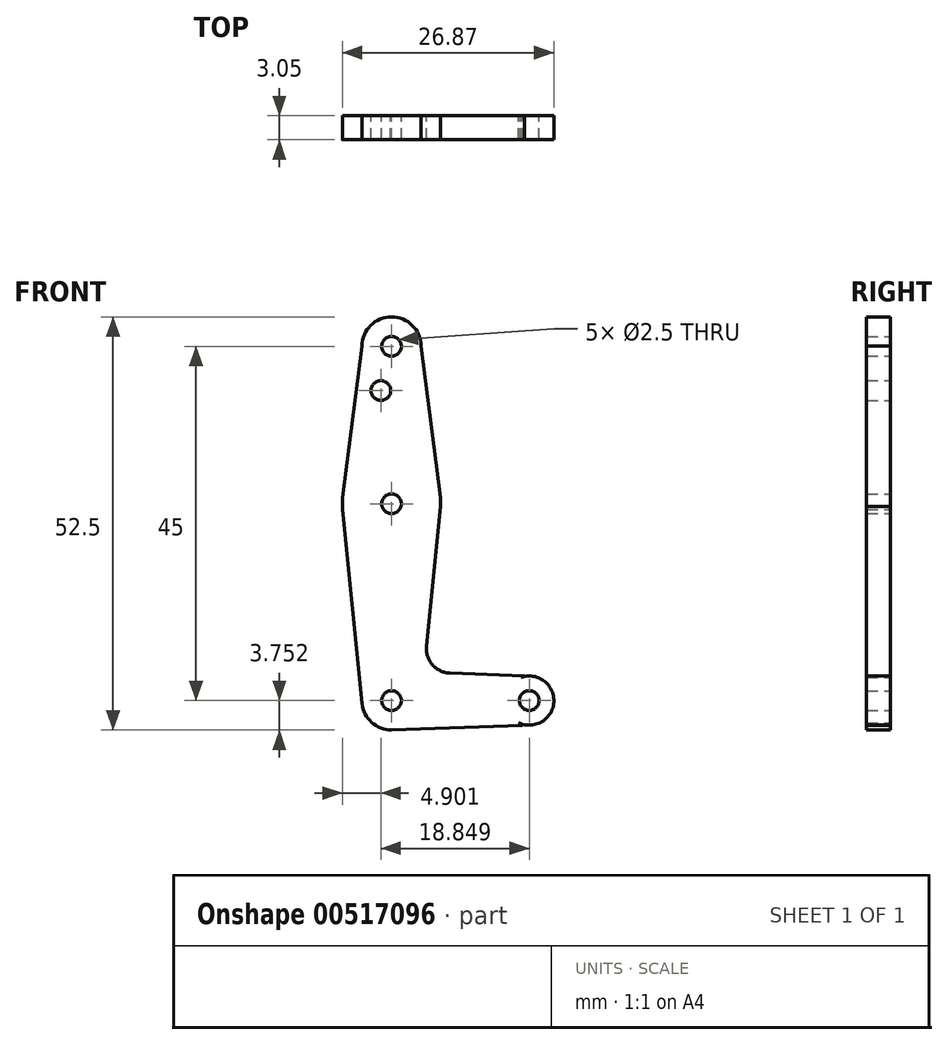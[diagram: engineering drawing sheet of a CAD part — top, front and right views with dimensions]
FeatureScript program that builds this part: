
annotation { "Feature Type Name" : "Feature", "Feature Type Description" : "" }
export const myFeature = defineFeature(function(context is Context, id is Id, definition is map)
    precondition{}
    {
        {
            var Q0;
            Q0=qCreatedBy(makeId("Front.planeOp"),FACE);
            var sketch = newSketch(context, id + "F0", { "sketchPlane" : qUnion([Q0])});
            skLineSegment(sketch, "E0", {"start": v(-17.5, -53.76) * mm, "end": v(-17.5, -28.76) * mm});
            skLineSegment(sketch, "E1", {"start": v(-17.5, -28.76) * mm, "end": v(-17.5, -8.76) * mm});
            skLineSegment(sketch, "E2", {"start": v(-17.5, -53.76) * mm, "end": v(0, -53.76) * mm});
            skCircle(sketch, "E3", {"center": v(-17.5, -8.76) * mm, "radius": 3.75 * mm});
            skCircle(sketch, "E4", {"center": v(-17.5, -28.76) * mm, "radius": 6.25 * mm});
            skCircle(sketch, "E5", {"center": v(-17.5, -53.76) * mm, "radius": 3.75 * mm});
            skCircle(sketch, "E6", {"center": v(0, -53.76) * mm, "radius": 3.12 * mm});
            skLineSegment(sketch, "E7", {"start": v(-21.25, -8.7) * mm, "end": v(-23.7, -27.97) * mm});
            skLineSegment(sketch, "E8", {"start": v(-13.75, -8.7) * mm, "end": v(-11.3, -27.97) * mm});
            skLineSegment(sketch, "E9", {"start": v(-23.7, -29.5) * mm, "end": v(-21.23, -54.13) * mm});
            skLineSegment(sketch, "E10", {"start": v(-11.26, -29.13) * mm, "end": v(-13.05, -46.83) * mm});
            skLineSegment(sketch, "E11", {"start": v(-10.05, -50.27) * mm, "end": v(0, -50.63) * mm});
            skLineSegment(sketch, "E12", {"start": v(-17.5, -57.5) * mm, "end": v(0, -56.89) * mm});
            skCircle(sketch, "E13", {"center": v(-17.5, -8.76) * mm, "radius": 1.25 * mm});
            skCircle(sketch, "E14", {"center": v(-17.5, -28.76) * mm, "radius": 1.25 * mm});
            skCircle(sketch, "E15", {"center": v(-17.5, -53.76) * mm, "radius": 1.25 * mm});
            skCircle(sketch, "E16", {"center": v(0, -53.76) * mm, "radius": 1.25 * mm});
            skArc(sketch, "E17.filletArc", {"start": v(-13.05, -46.83) * mm, "mid": v(-12.3, -49.2) * mm, "end": v(-10.05, -50.27) * mm});
            skCircle(sketch, "E18", {"center": v(-18.85, -14.38) * mm, "radius": 1.25 * mm});
            skLineSegment(sketch, "E19", {"start": v(-0.6, -50.6) * mm, "end": v(-1.03, -50.8) * mm});
            skLineSegment(sketch, "E20", {"start": v(-0.89, -56.92) * mm, "end": v(-1.35, -56.58) * mm});
            skSolve(sketch);
        }
        {
            var Q0;
            Q0=makeQuery(id+"F0.imprint","IMPRINT",FACE,{"disambiguationData":[TD([[makeQuery(id+"F0.imprint","IMPRINT",EDGE,{"derivedFrom":sQuery(id+"F0.wireOp",EDGE,"E13")}),-1.0]])]});
            var Q1;
            {var subQ5=sQuery(id+"F0.wireOp",EDGE,"E8");Q1=makeQuery(id+"F0.imprint","IMPRINT",FACE,{"disambiguationData":[TD([[makeQuery(id+"F0.imprint","IMPRINT",EDGE,{"derivedFrom":subQ5}),-1.0]])]});}
            var Q2;
            {var subQ0=sQuery(id+"F0.wireOp",EDGE,"E7");Q2=makeQuery(id+"F0.imprint","IMPRINT",FACE,{"disambiguationData":[TD([[makeQuery(id+"F0.imprint","IMPRINT",EDGE,{"derivedFrom":subQ0}),1.0]])]});}
            var Q3;
            {var subQ0=sQuery(id+"F0.wireOp",EDGE,"E4");var subQ6=sQuery(id+"F0.wireOp",EDGE,"E0");var subQ9=makeQuery(id+"F0.imprint","INTERSECT",VERTEX,{"derivedFrom":[subQ6,subQ0]});Q3=makeQuery(id+"F0.imprint","IMPRINT",FACE,{"disambiguationData":[TD([[makeQuery(id+"F0.imprint","IMPRINT",EDGE,{"disambiguationData":[TD([[subQ9,-1.0]])],"derivedFrom":subQ6}),1.0]])]});}
            var Q4;
            {var subQ0=sQuery(id+"F0.wireOp",EDGE,"E4");var subQ4=sQuery(id+"F0.wireOp",EDGE,"E0");var subQ5=makeQuery(id+"F0.imprint","INTERSECT",VERTEX,{"derivedFrom":[subQ4,subQ0]});Q4=makeQuery(id+"F0.imprint","IMPRINT",FACE,{"disambiguationData":[TD([[makeQuery(id+"F0.imprint","IMPRINT",EDGE,{"disambiguationData":[TD([[subQ5,-1.0]])],"derivedFrom":subQ4}),-1.0]])]});}
            var Q5;
            {var subQ5=sQuery(id+"F0.wireOp",EDGE,"E9");Q5=makeQuery(id+"F0.imprint","IMPRINT",FACE,{"disambiguationData":[TD([[makeQuery(id+"F0.imprint","IMPRINT",EDGE,{"derivedFrom":subQ5}),1.0]])]});}
            var Q6;
            {var subQ7=sQuery(id+"F0.wireOp",EDGE,"E17.filletArc");Q6=makeQuery(id+"F0.imprint","IMPRINT",FACE,{"disambiguationData":[TD([[makeQuery(id+"F0.imprint","IMPRINT",EDGE,{"derivedFrom":subQ7}),-1.0]])]});}
            var Q7;
            {var subQ0=sQuery(id+"F0.wireOp",EDGE,"E15");var subQ1=sQuery(id+"F0.wireOp",EDGE,"E0");var subQ2=makeQuery(id+"F0.imprint","INTERSECT",VERTEX,{"derivedFrom":[subQ1,subQ0]});Q7=makeQuery(id+"F0.imprint","IMPRINT",FACE,{"disambiguationData":[TD([[makeQuery(id+"F0.imprint","IMPRINT",EDGE,{"disambiguationData":[TD([[subQ2,-1.0]])],"derivedFrom":subQ1}),-1.0]])]});}
            var Q8;
            {var subQ4=sQuery(id+"F0.wireOp",EDGE,"E15");var subQ5=sQuery(id+"F0.wireOp",EDGE,"E0");var subQ6=makeQuery(id+"F0.imprint","INTERSECT",VERTEX,{"derivedFrom":[subQ5,subQ4]});Q8=makeQuery(id+"F0.imprint","IMPRINT",FACE,{"disambiguationData":[TD([[makeQuery(id+"F0.imprint","IMPRINT",EDGE,{"disambiguationData":[TD([[subQ6,-1.0]])],"derivedFrom":subQ5}),1.0]])]});}
            var Q9;
            {var subQ0=sQuery(id+"F0.wireOp",EDGE,"E20");Q9=makeQuery(id+"F0.imprint","IMPRINT",FACE,{"disambiguationData":[TD([[makeQuery(id+"F0.imprint","IMPRINT",EDGE,{"derivedFrom":subQ0}),1.0]])]});}
            var Q10;
            Q10=makeQuery(id+"F0.imprint","IMPRINT",FACE,{"disambiguationData":[TD([[makeQuery(id+"F0.imprint","IMPRINT",EDGE,{"derivedFrom":sQuery(id+"F0.wireOp",EDGE,"E16")}),-1.0]])]});
            extrude(context, id + "F1", {"entities" : qUnion([Q0, Q1, Q2, Q3, Q4, Q5, Q6, Q7, Q8, Q9, Q10]), "depth" : 3.05 * mm, "offsetDistance" : 25 * mm});
        }
    });
